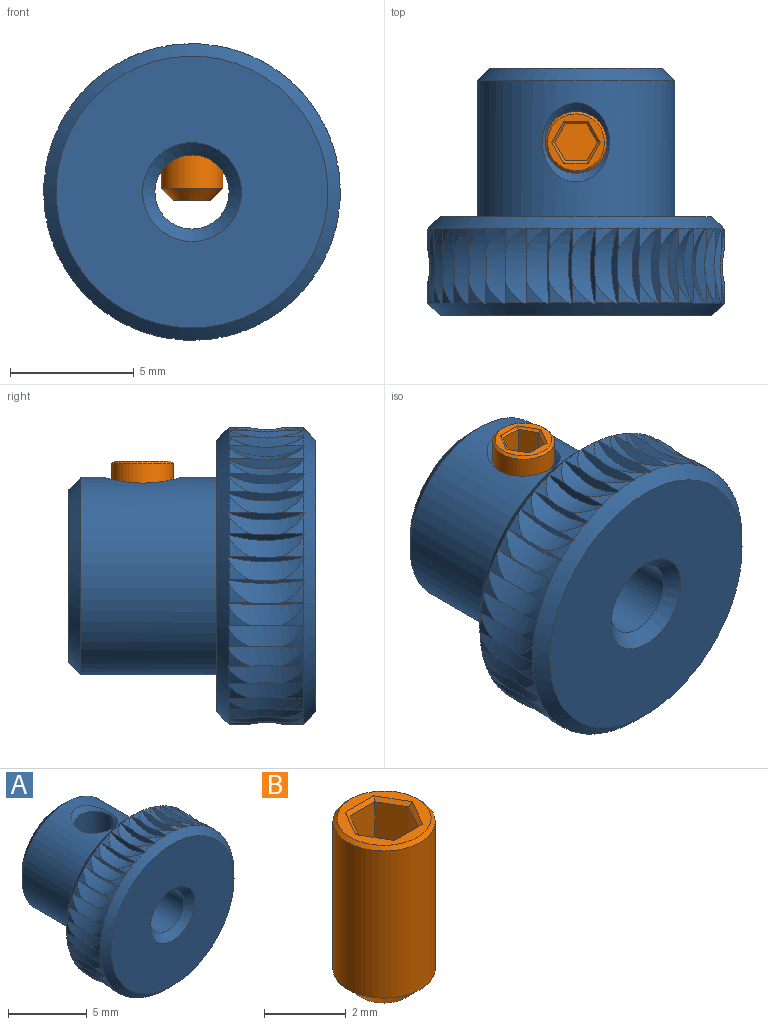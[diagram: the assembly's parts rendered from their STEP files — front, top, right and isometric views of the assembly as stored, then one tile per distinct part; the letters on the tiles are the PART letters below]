
ASSEMBLY  parts=2 mates=1
PART A: 172 faces, bbox 12.6x10x12.6 mm
  f0: cylinder r=1.5mm len=9mm, axis (0,-1,0), area 79.3mm2, adj f167,f168,f170
  f1: cylinder r=4mm len=8mm, axis (0,1,0), area 131.3mm2, adj f164,f165,f171
  f2: cylinder r=6mm len=0.84mm, axis (0,-1,0), area 0.3mm2, adj f156,f159,f169
  f3: cylinder r=6mm len=0.84mm, axis (0,-1,0), area 0.3mm2, adj f155,f158,f169
  f4: cylinder r=6mm len=0.84mm, axis (0,-1,0), area 0.3mm2, adj f148,f157,f169
  f5: cylinder r=6mm len=0.84mm, axis (0,-1,0), area 0.3mm2, adj f152,f154,f169
  f6: cylinder r=6mm len=0.84mm, axis (0,-1,0), area 0.3mm2, adj f149,f153,f169
  f7: cylinder r=6mm len=0.84mm, axis (0,-1,0), area 0.3mm2, adj f147,f151,f169
  f8: cylinder r=6mm len=0.84mm, axis (0,-1,0), area 0.3mm2, adj f84,f150,f169
  f9: cylinder r=6mm len=0.84mm, axis (0,-1,0), area 0.3mm2, adj f144,f146,f169
  f10: cylinder r=6mm len=0.84mm, axis (0,-1,0), area 0.3mm2, adj f141,f145,f169
  f11: cylinder r=6mm len=0.84mm, axis (0,-1,0), area 0.3mm2, adj f140,f143,f169
  f12: cylinder r=6mm len=0.84mm, axis (0,-1,0), area 0.3mm2, adj f133,f142,f169
  f13: cylinder r=6mm len=0.84mm, axis (0,-1,0), area 0.3mm2, adj f137,f139,f169
  f14: cylinder r=6mm len=0.84mm, axis (0,-1,0), area 0.3mm2, adj f134,f138,f169
  f15: cylinder r=6mm len=0.84mm, axis (0,-1,0), area 0.3mm2, adj f132,f136,f169
  f16: cylinder r=6mm len=0.84mm, axis (0,-1,0), area 0.3mm2, adj f117,f135,f169
  f17: cylinder r=6mm len=0.84mm, axis (0,-1,0), area 0.3mm2, adj f129,f131,f169
  f18: cylinder r=6mm len=0.84mm, axis (0,-1,0), area 0.3mm2, adj f126,f130,f169
  f19: cylinder r=6mm len=0.84mm, axis (0,-1,0), area 0.3mm2, adj f125,f128,f169
  f20: cylinder r=6mm len=0.84mm, axis (0,-1,0), area 0.3mm2, adj f118,f127,f169
  f21: cylinder r=6mm len=0.84mm, axis (0,-1,0), area 0.3mm2, adj f122,f124,f169
  f22: cylinder r=6mm len=0.84mm, axis (0,-1,0), area 0.3mm2, adj f119,f123,f169
  f23: cylinder r=6mm len=0.84mm, axis (0,-1,0), area 0.3mm2, adj f116,f121,f169
  f24: cylinder r=6mm len=0.84mm, axis (0,-1,0), area 0.3mm2, adj f85,f120,f169
  f25: cylinder r=6mm len=0.84mm, axis (0,-1,0), area 0.3mm2, adj f113,f115,f169
  f26: cylinder r=6mm len=0.84mm, axis (0,-1,0), area 0.3mm2, adj f110,f114,f169
  f27: cylinder r=6mm len=0.84mm, axis (0,-1,0), area 0.3mm2, adj f109,f112,f169
  f28: cylinder r=6mm len=0.84mm, axis (0,-1,0), area 0.3mm2, adj f102,f111,f169
  f29: cylinder r=6mm len=0.84mm, axis (0,-1,0), area 0.3mm2, adj f106,f108,f169
  f30: cylinder r=6mm len=0.84mm, axis (0,-1,0), area 0.3mm2, adj f103,f107,f169
  f31: cylinder r=6mm len=0.84mm, axis (0,-1,0), area 0.3mm2, adj f101,f105,f169
  f32: cylinder r=6mm len=0.84mm, axis (0,-1,0), area 0.3mm2, adj f86,f104,f169
  f33: cylinder r=6mm len=0.84mm, axis (0,-1,0), area 0.3mm2, adj f98,f100,f169
  f34: cylinder r=6mm len=0.84mm, axis (0,-1,0), area 0.3mm2, adj f95,f99,f169
  f35: cylinder r=6mm len=0.84mm, axis (0,-1,0), area 0.3mm2, adj f94,f97,f169
  f36: cylinder r=6mm len=0.84mm, axis (0,-1,0), area 0.3mm2, adj f87,f96,f169
  f37: cylinder r=6mm len=0.84mm, axis (0,-1,0), area 0.3mm2, adj f91,f93,f169
  f38: cylinder r=6mm len=0.84mm, axis (0,-1,0), area 0.3mm2, adj f88,f92,f169
  f39: cylinder r=6mm len=0.84mm, axis (0,-1,0), area 0.3mm2, adj f82,f90,f169
  f40: cylinder r=6mm len=0.84mm, axis (0,-1,0), area 0.3mm2, adj f89,f160,f169
  f41: cylinder r=6mm len=0.84mm, axis (0,-1,0), area 0.3mm2, adj f149,f153,f166
  f42: cylinder r=6mm len=0.84mm, axis (0,-1,0), area 0.3mm2, adj f152,f154,f166
  f43: cylinder r=6mm len=0.84mm, axis (0,-1,0), area 0.3mm2, adj f148,f157,f166
  f44: cylinder r=6mm len=0.84mm, axis (0,-1,0), area 0.3mm2, adj f155,f158,f166
  f45: cylinder r=6mm len=0.84mm, axis (0,-1,0), area 0.3mm2, adj f156,f159,f166
  f46: cylinder r=6mm len=0.84mm, axis (0,-1,0), area 0.3mm2, adj f83,f161,f166
  f47: cylinder r=6mm len=0.84mm, axis (0,-1,0), area 0.3mm2, adj f89,f160,f166
  f48: cylinder r=6mm len=0.84mm, axis (0,-1,0), area 0.3mm2, adj f82,f90,f166
  f49: cylinder r=6mm len=0.84mm, axis (0,-1,0), area 0.3mm2, adj f88,f92,f166
  f50: cylinder r=6mm len=0.84mm, axis (0,-1,0), area 0.3mm2, adj f91,f93,f166
  f51: cylinder r=6mm len=0.84mm, axis (0,-1,0), area 0.3mm2, adj f87,f96,f166
  f52: cylinder r=6mm len=0.84mm, axis (0,-1,0), area 0.3mm2, adj f94,f97,f166
  f53: cylinder r=6mm len=0.84mm, axis (0,-1,0), area 0.3mm2, adj f95,f99,f166
  f54: cylinder r=6mm len=0.84mm, axis (0,-1,0), area 0.3mm2, adj f98,f100,f166
  f55: cylinder r=6mm len=0.84mm, axis (0,-1,0), area 0.3mm2, adj f86,f104,f166
  f56: cylinder r=6mm len=0.84mm, axis (0,-1,0), area 0.3mm2, adj f101,f105,f166
  f57: cylinder r=6mm len=0.84mm, axis (0,-1,0), area 0.3mm2, adj f103,f107,f166
  f58: cylinder r=6mm len=0.84mm, axis (0,-1,0), area 0.3mm2, adj f106,f108,f166
  f59: cylinder r=6mm len=0.84mm, axis (0,-1,0), area 0.3mm2, adj f102,f111,f166
  f60: cylinder r=6mm len=0.84mm, axis (0,-1,0), area 0.3mm2, adj f109,f112,f166
  f61: cylinder r=6mm len=0.84mm, axis (0,-1,0), area 0.3mm2, adj f110,f114,f166
  f62: cylinder r=6mm len=0.84mm, axis (0,-1,0), area 0.3mm2, adj f113,f115,f166
  f63: cylinder r=6mm len=0.84mm, axis (0,-1,0), area 0.3mm2, adj f85,f120,f166
  f64: cylinder r=6mm len=0.84mm, axis (0,-1,0), area 0.3mm2, adj f116,f121,f166
  f65: cylinder r=6mm len=0.84mm, axis (0,-1,0), area 0.3mm2, adj f119,f123,f166
  f66: cylinder r=6mm len=0.84mm, axis (0,-1,0), area 0.3mm2, adj f122,f124,f166
  f67: cylinder r=6mm len=0.84mm, axis (0,-1,0), area 0.3mm2, adj f118,f127,f166
  f68: cylinder r=6mm len=0.84mm, axis (0,-1,0), area 0.3mm2, adj f125,f128,f166
  f69: cylinder r=6mm len=0.84mm, axis (0,-1,0), area 0.3mm2, adj f126,f130,f166
  f70: cylinder r=6mm len=0.84mm, axis (0,-1,0), area 0.3mm2, adj f129,f131,f166
  f71: cylinder r=6mm len=0.84mm, axis (0,-1,0), area 0.3mm2, adj f117,f135,f166
  f72: cylinder r=6mm len=0.84mm, axis (0,-1,0), area 0.3mm2, adj f132,f136,f166
  f73: cylinder r=6mm len=0.84mm, axis (0,-1,0), area 0.3mm2, adj f134,f138,f166
  f74: cylinder r=6mm len=0.84mm, axis (0,-1,0), area 0.3mm2, adj f137,f139,f166
  f75: cylinder r=6mm len=0.84mm, axis (0,-1,0), area 0.3mm2, adj f133,f142,f166
  f76: cylinder r=6mm len=0.84mm, axis (0,-1,0), area 0.3mm2, adj f140,f143,f166
  f77: cylinder r=6mm len=0.84mm, axis (0,-1,0), area 0.3mm2, adj f141,f145,f166
  f78: cylinder r=6mm len=0.84mm, axis (0,-1,0), area 0.3mm2, adj f144,f146,f166
  f79: cylinder r=6mm len=0.84mm, axis (0,-1,0), area 0.3mm2, adj f84,f150,f166
  f80: cylinder r=6mm len=0.84mm, axis (0,-1,0), area 0.3mm2, adj f147,f151,f166
  f81: plane 7x7mm, normal (0,1,0), area 25.9mm2, adj f165,f167
  f82: cylinder r=3mm len=3.07mm, axis (0.16,0,-0.99), area 2.2mm2, adj f39,f48,f89,f90,f166,f169
  f83: cylinder r=3mm len=3.07mm, axis (-0.16,0,-0.99), area 2.2mm2, adj f46,f159,f161,f163,f166,f169
  f84: cylinder r=3mm len=3.07mm, axis (-0.95,0,-0.31), area 2.2mm2, adj f8,f79,f146,f150,f166,f169
  f85: cylinder r=3mm len=3.07mm, axis (0.59,0,0.81), area 2.2mm2, adj f24,f63,f115,f120,f166,f169
  f86: cylinder r=3mm len=3.07mm, axis (0.95,0,-0.31), area 2.2mm2, adj f32,f55,f100,f104,f166,f169
  f87: cylinder r=3mm len=3.07mm, axis (0.59,0,-0.81), area 2.2mm2, adj f36,f51,f93,f96,f166,f169
  f88: cylinder r=3mm len=3.07mm, axis (0.31,0,-0.95), area 2.2mm2, adj f38,f49,f90,f92,f166,f169
  f89: plane 3.09x0.47mm, normal (-0.16,0,0.99), area 0.9mm2, adj f40,f47,f82,f160,f166,f169
  f90: plane 3.09x0.46mm, normal (-0.31,0,0.95), area 0.9mm2, adj f39,f48,f82,f88,f166,f169
  f91: cylinder r=3mm len=3.07mm, axis (0.45,0,-0.89), area 2.2mm2, adj f37,f50,f92,f93,f166,f169
  f92: plane 3.09x0.43mm, normal (-0.45,0,0.89), area 0.9mm2, adj f38,f49,f88,f91,f166,f169
  f93: plane 3.09x0.39mm, normal (-0.59,0,0.81), area 0.9mm2, adj f37,f50,f87,f91,f166,f169
  f94: cylinder r=3mm len=3.07mm, axis (0.71,0,-0.71), area 2.2mm2, adj f35,f52,f96,f97,f166,f169
  f95: cylinder r=3mm len=3.07mm, axis (0.81,0,-0.59), area 2.2mm2, adj f34,f53,f97,f99,f166,f169
  f96: plane 3.09x0.35mm, normal (-0.71,0,0.71), area 0.9mm2, adj f36,f51,f87,f94,f166,f169
  f97: plane 3.09x0.39mm, normal (-0.81,0,0.59), area 0.9mm2, adj f35,f52,f94,f95,f166,f169
  f98: cylinder r=3mm len=3.07mm, axis (0.89,0,-0.45), area 2.2mm2, adj f33,f54,f99,f100,f166,f169
  f99: plane 3.09x0.43mm, normal (-0.89,0,0.45), area 0.9mm2, adj f34,f53,f95,f98,f166,f169
  f100: plane 3.09x0.46mm, normal (-0.95,0,0.31), area 0.9mm2, adj f33,f54,f86,f98,f166,f169
  f101: cylinder r=3mm len=3.07mm, axis (0.99,0,-0.16), area 2.2mm2, adj f31,f56,f104,f105,f166,f169
  f102: cylinder r=3mm len=3.07mm, axis (0.95,0,0.31), area 2.2mm2, adj f28,f59,f108,f111,f166,f169
  f103: cylinder r=3mm len=3.07mm, axis (1,0,0), area 2.2mm2, adj f30,f57,f105,f107,f166,f169
  f104: plane 3.09x0.47mm, normal (-0.99,0,0.16), area 0.9mm2, adj f32,f55,f86,f101,f166,f169
  f105: plane 3.09x0.48mm, normal (-1,0,0), area 0.9mm2, adj f31,f56,f101,f103,f166,f169
  f106: cylinder r=3mm len=3.07mm, axis (0.99,0,0.16), area 2.2mm2, adj f29,f58,f107,f108,f166,f169
  f107: plane 3.09x0.47mm, normal (-0.99,0,-0.16), area 0.9mm2, adj f30,f57,f103,f106,f166,f169
  f108: plane 3.09x0.46mm, normal (-0.95,0,-0.31), area 0.9mm2, adj f29,f58,f102,f106,f166,f169
  f109: cylinder r=3mm len=3.07mm, axis (0.89,0,0.45), area 2.2mm2, adj f27,f60,f111,f112,f166,f169
  f110: cylinder r=3mm len=3.07mm, axis (0.81,0,0.59), area 2.2mm2, adj f26,f61,f112,f114,f166,f169
  f111: plane 3.09x0.43mm, normal (-0.89,0,-0.45), area 0.9mm2, adj f28,f59,f102,f109,f166,f169
  f112: plane 3.09x0.39mm, normal (-0.81,0,-0.59), area 0.9mm2, adj f27,f60,f109,f110,f166,f169
  f113: cylinder r=3mm len=3.07mm, axis (0.71,0,0.71), area 2.2mm2, adj f25,f62,f114,f115,f166,f169
  f114: plane 3.09x0.35mm, normal (-0.71,0,-0.71), area 0.9mm2, adj f26,f61,f110,f113,f166,f169
  f115: plane 3.09x0.39mm, normal (-0.59,0,-0.81), area 0.9mm2, adj f25,f62,f85,f113,f166,f169
  f116: cylinder r=3mm len=3.07mm, axis (0.45,0,0.89), area 2.2mm2, adj f23,f64,f120,f121,f166,f169
  f117: cylinder r=3mm len=3.07mm, axis (-0.59,0,0.81), area 2.2mm2, adj f16,f71,f131,f135,f166,f169
  f118: cylinder r=3mm len=3.07mm, axis (0,0,1), area 2.2mm2, adj f20,f67,f124,f127,f166,f169
  f119: cylinder r=3mm len=3.07mm, axis (0.31,0,0.95), area 2.2mm2, adj f22,f65,f121,f123,f166,f169
  f120: plane 3.09x0.43mm, normal (-0.45,0,-0.89), area 0.9mm2, adj f24,f63,f85,f116,f166,f169
  f121: plane 3.09x0.46mm, normal (-0.31,0,-0.95), area 0.9mm2, adj f23,f64,f116,f119,f166,f169
  f122: cylinder r=3mm len=3.07mm, axis (0.16,0,0.99), area 2.2mm2, adj f21,f66,f123,f124,f166,f169
  f123: plane 3.09x0.47mm, normal (-0.16,0,-0.99), area 0.9mm2, adj f22,f65,f119,f122,f166,f169
  f124: plane 3.09x0.48mm, normal (0,0,-1), area 0.9mm2, adj f21,f66,f118,f122,f166,f169
  f125: cylinder r=3mm len=3.07mm, axis (-0.16,0,0.99), area 2.2mm2, adj f19,f68,f127,f128,f166,f169
  f126: cylinder r=3mm len=3.07mm, axis (-0.31,0,0.95), area 2.2mm2, adj f18,f69,f128,f130,f166,f169
  f127: plane 3.09x0.47mm, normal (0.16,0,-0.99), area 0.9mm2, adj f20,f67,f118,f125,f166,f169
  f128: plane 3.09x0.46mm, normal (0.31,0,-0.95), area 0.9mm2, adj f19,f68,f125,f126,f166,f169
  f129: cylinder r=3mm len=3.07mm, axis (-0.45,0,0.89), area 2.2mm2, adj f17,f70,f130,f131,f166,f169
  f130: plane 3.09x0.43mm, normal (0.45,0,-0.89), area 0.9mm2, adj f18,f69,f126,f129,f166,f169
  f131: plane 3.09x0.39mm, normal (0.59,0,-0.81), area 0.9mm2, adj f17,f70,f117,f129,f166,f169
  f132: cylinder r=3mm len=3.07mm, axis (-0.71,0,0.71), area 2.2mm2, adj f15,f72,f135,f136,f166,f169
  f133: cylinder r=3mm len=3.07mm, axis (-0.95,0,0.31), area 2.2mm2, adj f12,f75,f139,f142,f166,f169
  f134: cylinder r=3mm len=3.07mm, axis (-0.81,0,0.59), area 2.2mm2, adj f14,f73,f136,f138,f166,f169
  f135: plane 3.09x0.35mm, normal (0.71,0,-0.71), area 0.9mm2, adj f16,f71,f117,f132,f166,f169
  f136: plane 3.09x0.39mm, normal (0.81,0,-0.59), area 0.9mm2, adj f15,f72,f132,f134,f166,f169
  f137: cylinder r=3mm len=3.07mm, axis (-0.89,0,0.45), area 2.2mm2, adj f13,f74,f138,f139,f166,f169
  f138: plane 3.09x0.43mm, normal (0.89,0,-0.45), area 0.9mm2, adj f14,f73,f134,f137,f166,f169
  f139: plane 3.09x0.46mm, normal (0.95,0,-0.31), area 0.9mm2, adj f13,f74,f133,f137,f166,f169
  f140: cylinder r=3mm len=3.07mm, axis (-0.99,0,0.16), area 2.2mm2, adj f11,f76,f142,f143,f166,f169
  f141: cylinder r=3mm len=3.07mm, axis (-1,0,0), area 2.2mm2, adj f10,f77,f143,f145,f166,f169
  f142: plane 3.09x0.47mm, normal (0.99,0,-0.16), area 0.9mm2, adj f12,f75,f133,f140,f166,f169
  f143: plane 3.09x0.48mm, normal (1,0,0), area 0.9mm2, adj f11,f76,f140,f141,f166,f169
  f144: cylinder r=3mm len=3.07mm, axis (-0.99,0,-0.16), area 2.2mm2, adj f9,f78,f145,f146,f166,f169
  f145: plane 3.09x0.47mm, normal (0.99,0,0.16), area 0.9mm2, adj f10,f77,f141,f144,f166,f169
  f146: plane 3.09x0.46mm, normal (0.95,0,0.31), area 0.9mm2, adj f9,f78,f84,f144,f166,f169
  f147: cylinder r=3mm len=3.07mm, axis (-0.89,0,-0.45), area 2.2mm2, adj f7,f80,f150,f151,f166,f169
  f148: cylinder r=3mm len=3.07mm, axis (-0.59,0,-0.81), area 2.2mm2, adj f4,f43,f154,f157,f166,f169
  f149: cylinder r=3mm len=3.07mm, axis (-0.81,0,-0.59), area 2.2mm2, adj f6,f41,f151,f153,f166,f169
  f150: plane 3.09x0.43mm, normal (0.89,0,0.45), area 0.9mm2, adj f8,f79,f84,f147,f166,f169
  f151: plane 3.09x0.39mm, normal (0.81,0,0.59), area 0.9mm2, adj f7,f80,f147,f149,f166,f169
  f152: cylinder r=3mm len=3.07mm, axis (-0.71,0,-0.71), area 2.2mm2, adj f5,f42,f153,f154,f166,f169
  f153: plane 3.09x0.35mm, normal (0.71,0,0.71), area 0.9mm2, adj f6,f41,f149,f152,f166,f169
  f154: plane 3.09x0.39mm, normal (0.59,0,0.81), area 0.9mm2, adj f5,f42,f148,f152,f166,f169
  f155: cylinder r=3mm len=3.07mm, axis (-0.45,0,-0.89), area 2.2mm2, adj f3,f44,f157,f158,f166,f169
  f156: cylinder r=3mm len=3.07mm, axis (-0.31,0,-0.95), area 2.2mm2, adj f2,f45,f158,f159,f166,f169
  f157: plane 3.09x0.43mm, normal (0.45,0,0.89), area 0.9mm2, adj f4,f43,f148,f155,f166,f169
  f158: plane 3.09x0.46mm, normal (0.31,0,0.95), area 0.9mm2, adj f3,f44,f155,f156,f166,f169
  f159: plane 3.09x0.47mm, normal (0.16,0,0.99), area 0.9mm2, adj f2,f45,f83,f156,f166,f169
  f160: cylinder r=3mm len=3.07mm, axis (0,0,-1), area 2.2mm2, adj f40,f47,f89,f161,f166,f169
  f161: plane 3.09x0.48mm, normal (0,0,1), area 0.9mm2, adj f46,f83,f160,f163,f166,f169
  f162: plane 11x11mm, normal (0,-1,0), area 82.5mm2, adj f168,f169
  f163: cylinder r=6mm len=0.84mm, axis (0,-1,0), area 0.3mm2, adj f83,f161,f169
  f164: plane 11x11mm, normal (0,1,0), area 44.8mm2, adj f1,f166
  f165: cone r=3.5mm half-angle=45deg, axis (0,-1,0), area 16.7mm2, adj f1,f81
  f166: cone r=6mm half-angle=45deg, axis (0,-1,0), area 25.4mm2, adj f41,f42,f43,f44,f45,f46,f47,f48
  f167: cone r=1.5mm half-angle=45deg, axis (0,1,0), area 7.8mm2, adj f0,f81
  f168: cone r=1.5mm half-angle=45deg, axis (0,-1,0), area 7.8mm2, adj f0,f162
  f169: cone r=5.5mm half-angle=45deg, axis (0,1,0), area 25.4mm2, adj f2,f3,f4,f5,f6,f7,f8,f9
  f170: cylinder r=1.25mm len=2.82mm, axis (0,0,1), area 19.3mm2, adj f0,f171
  f171: cone r=1.25mm half-angle=45deg, axis (0,0,1), area 2.7mm2, adj f1,f170
PART B: 18 faces, bbox 2.5x2.5x5 mm
  f0: plane 2.3x2.3mm, normal (0,0,1), area 1.7mm2, adj f10,f11,f12,f13,f14,f15,f16
  f1: cylinder r=1.25mm len=4.4mm, axis (0,0,1), area 34.6mm2, adj f16,f17
  f2: plane 1.5x1.5mm, normal (0,0,-1), area 1.8mm2, adj f17
  f3: plane 1.4x0.75mm, normal (0.87,-0.5,0), area 1.2mm2, adj f4,f8,f9,f15
  f4: plane 1.4x0.75mm, normal (0.87,0.5,0), area 1.2mm2, adj f3,f5,f9,f13
  f5: plane 1.4x0.87mm, normal (0,1,0), area 1.2mm2, adj f4,f6,f9,f11
  f6: plane 1.4x0.75mm, normal (-0.87,0.5,0), area 1.2mm2, adj f5,f7,f9,f10
  f7: plane 1.4x0.75mm, normal (-0.87,-0.5,0), area 1.2mm2, adj f6,f8,f9,f12
  f8: plane 1.4x0.87mm, normal (0,-1,0), area 1.2mm2, adj f3,f7,f9,f14
  f9: plane 1.73x1.5mm, normal (0,0,1), area 1.9mm2, adj f3,f4,f5,f6,f7,f8
  f10: plane 0.85x0.55mm, normal (-0.61,0.35,0.71), area 0.1mm2, adj f0,f6,f11,f12
  f11: plane 0.98x0.1mm, normal (0,0.71,0.71), area 0.1mm2, adj f0,f5,f10,f13
  f12: plane 0.85x0.55mm, normal (-0.61,-0.35,0.71), area 0.1mm2, adj f0,f7,f10,f14
  f13: plane 0.85x0.55mm, normal (0.61,0.35,0.71), area 0.1mm2, adj f0,f4,f11,f15
  f14: plane 0.98x0.1mm, normal (0,-0.71,0.71), area 0.1mm2, adj f0,f8,f12,f15
  f15: plane 0.85x0.55mm, normal (0.61,-0.35,0.71), area 0.1mm2, adj f0,f3,f13,f14
  f16: cone r=1.15mm half-angle=45deg, axis (0,0,-1), area 1.1mm2, adj f0,f1
  f17: cone r=1.25mm half-angle=45deg, axis (0,0,1), area 4.4mm2, adj f1,f2
PLACE A t=(-2.84,-6.02,2.93)mm
PLACE B t=(-2.84,0.98,5.58)mm
MATE fastened B.f1 <-> A.f170  axis (0,0,1) through (-2.84,0.98,5.58)mm
